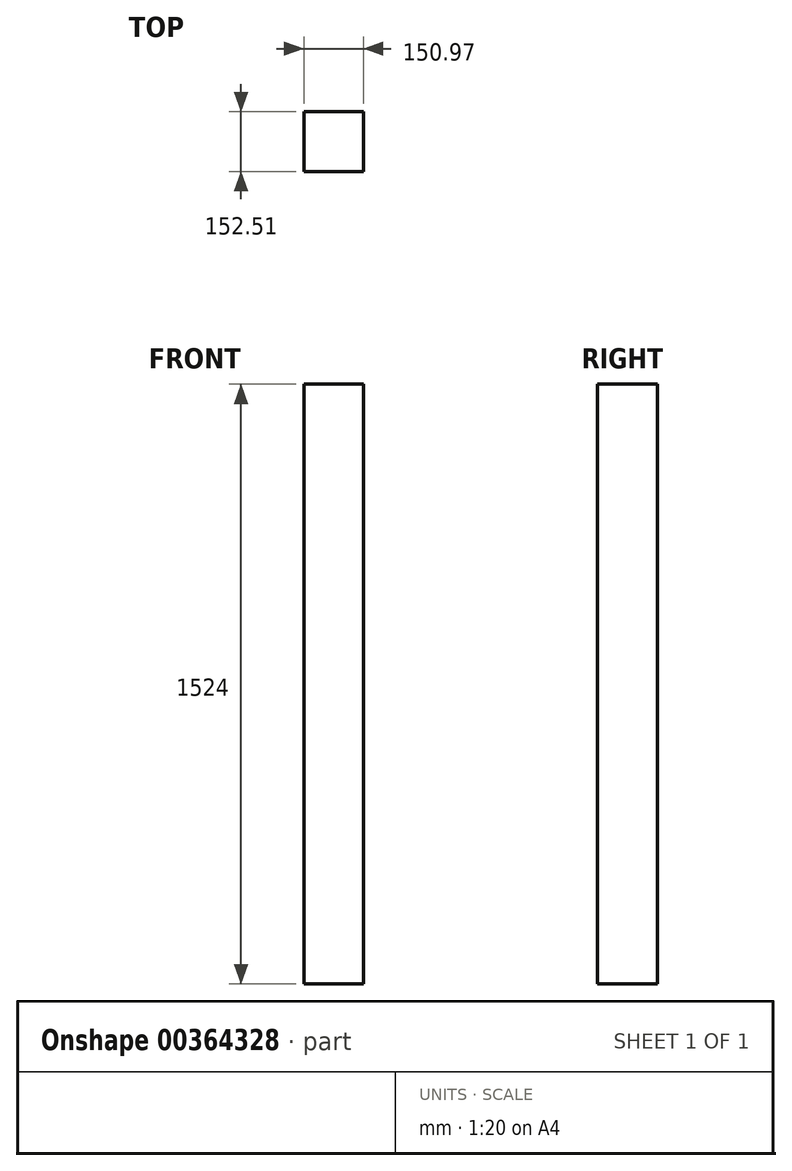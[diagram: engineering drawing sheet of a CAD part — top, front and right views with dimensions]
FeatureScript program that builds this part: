
annotation { "Feature Type Name" : "Feature", "Feature Type Description" : "" }
export const myFeature = defineFeature(function(context is Context, id is Id, definition is map)
    precondition{}
    {
        {
            var Q0;
            Q0=qCreatedBy(makeId("Top.planeOp"),FACE);
            var sketch = newSketch(context, id + "F0", { "sketchPlane" : qUnion([Q0])});
            skLineSegment(sketch, "E0.bottom", {"start": v(-75.4, -75.89) * mm, "end": v(75.57, -75.89) * mm});
            skLineSegment(sketch, "E0.top", {"start": v(-75.4, 76.62) * mm, "end": v(75.57, 76.62) * mm});
            skLineSegment(sketch, "E0.left", {"start": v(-75.4, -75.89) * mm, "end": v(-75.4, 76.62) * mm});
            skLineSegment(sketch, "E0.right", {"start": v(75.57, -75.89) * mm, "end": v(75.57, 76.62) * mm});
            skSolve(sketch);
        }
        {
            var Q0;
            Q0 = qSketchRegion(id + "F0", true);
            extrude(context, id + "F1", {"entities" : qUnion([Q0]), "depth" : 1524 * mm});
        }
        {
            var Q0;
            Q0=makeQuery(id+"F1.opExtrude","SWEPT_FACE",FACE,{"disambiguationData":[OSD([sQuery(id+"F0.wireOp",EDGE,"E0.left")])]});
            var sketch = newSketch(context, id + "F2", { "sketchPlane" : qUnion([Q0])});
            skPoint(sketch, "E1.oppositeSnap0", {"position": v(-76.62, 762) * mm});
            skLineSegment(sketch, "E1.bottom", {"start": v(0, 1307.24) * mm, "end": v(0, 1307.24) * mm});
            skLineSegment(sketch, "E1.top", {"start": v(0, 762) * mm, "end": v(0, 762) * mm});
            skLineSegment(sketch, "E1.left", {"start": v(0, 1307.24) * mm, "end": v(0, 762) * mm});
            skLineSegment(sketch, "E1.right", {"start": v(0, 1307.24) * mm, "end": v(0, 762) * mm});
            skSolve(sketch);
        }
        {
            var Q0;
            Q0=sQuery(id+"F2.wireOp",EDGE,"E1.right");
            extrude(context, id + "F3", {"bodyType" : ToolBodyType.SURFACE, "surfaceEntities" : qUnion([Q0]), "depth" : 609.6 * mm});
        }
    });
